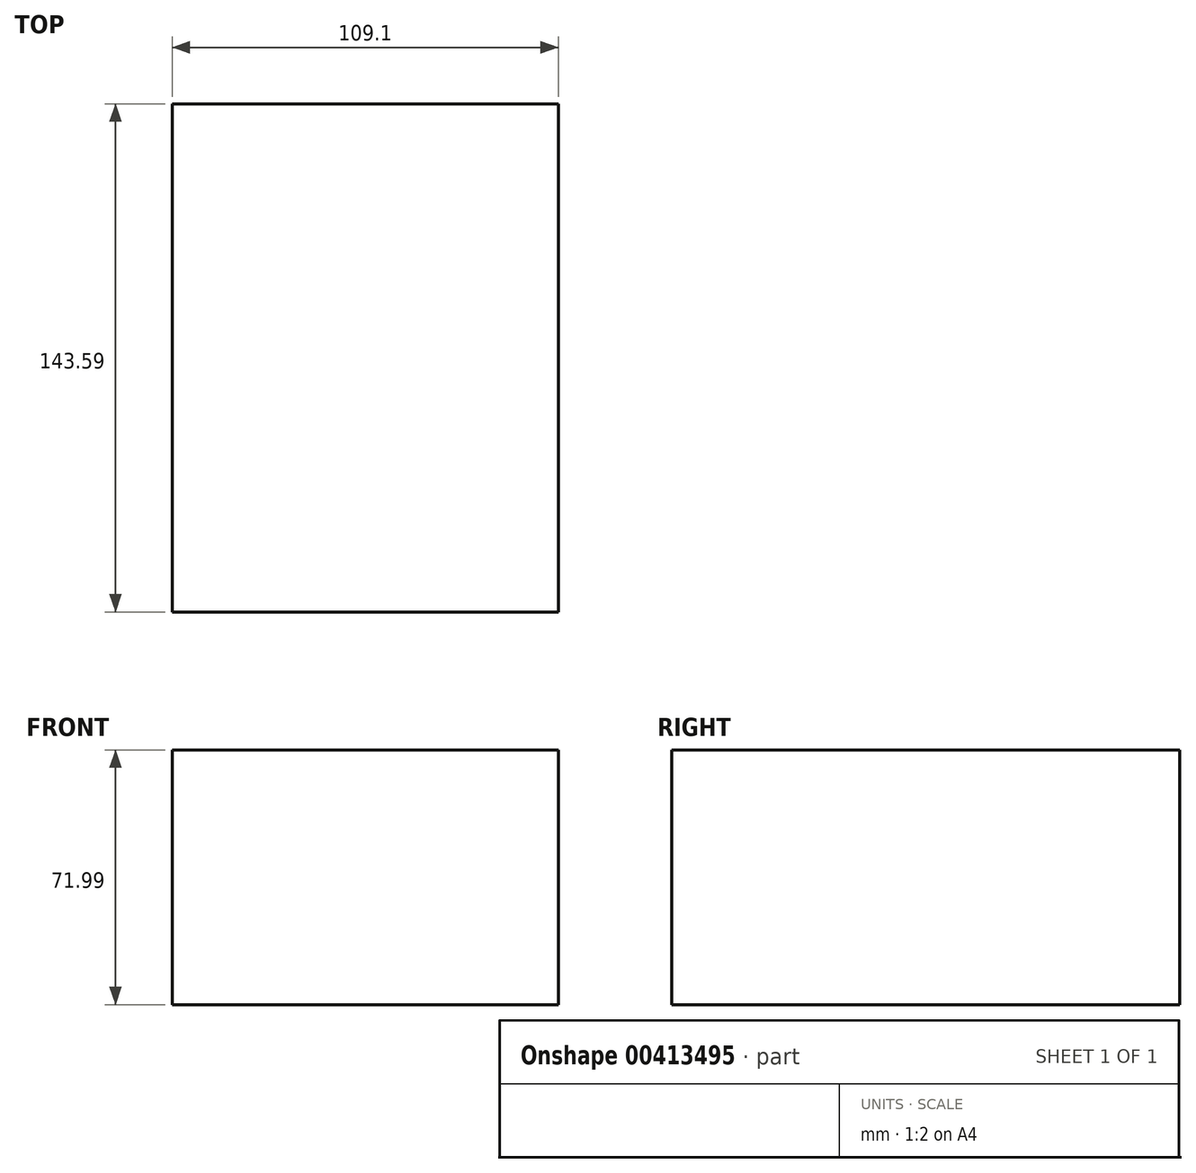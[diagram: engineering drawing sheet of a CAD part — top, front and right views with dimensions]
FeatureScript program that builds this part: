
annotation { "Feature Type Name" : "Feature", "Feature Type Description" : "" }
export const myFeature = defineFeature(function(context is Context, id is Id, definition is map)
    precondition{}
    {
        {
            var Q0;
            Q0=qCreatedBy(makeId("Top.planeOp"),FACE);
            var sketch = newSketch(context, id + "F0", { "sketchPlane" : qUnion([Q0])});
            skLineSegment(sketch, "E0.bottom", {"start": v(69, 143.59) * mm, "end": v(-40.1, 143.59) * mm});
            skLineSegment(sketch, "E0.top", {"start": v(69, 0) * mm, "end": v(-40.1, 0) * mm});
            skLineSegment(sketch, "E0.left", {"start": v(69, 143.59) * mm, "end": v(69, 0) * mm});
            skLineSegment(sketch, "E0.right", {"start": v(-40.1, 143.59) * mm, "end": v(-40.1, 0) * mm});
            skSolve(sketch);
        }
        {
            var Q0;
            Q0 = qSketchRegion(id + "F0", true);
            extrude(context, id + "F1", {"entities" : qUnion([Q0]), "depth" : 72 * mm});
        }
    });
